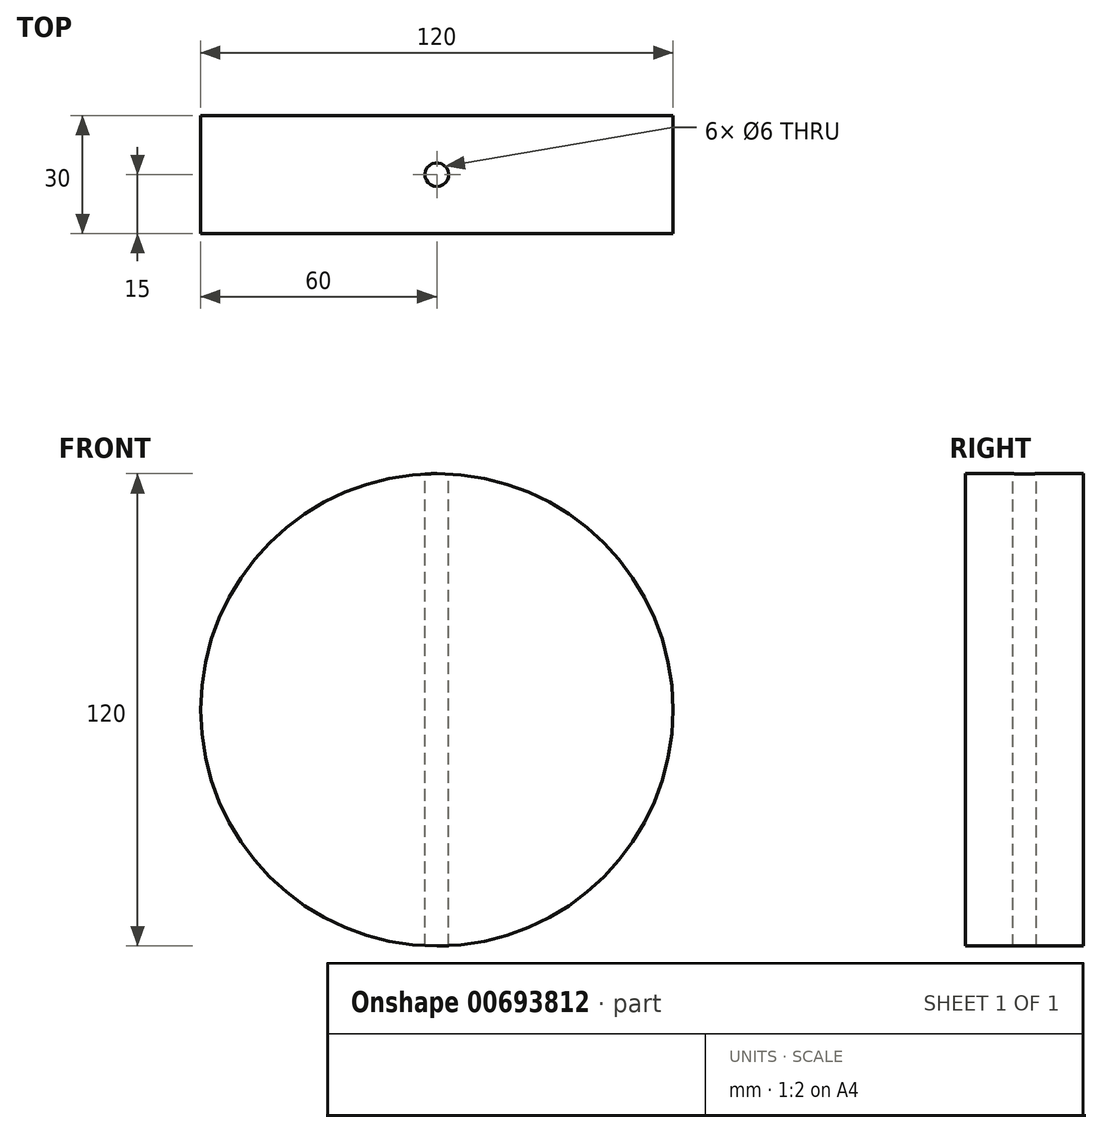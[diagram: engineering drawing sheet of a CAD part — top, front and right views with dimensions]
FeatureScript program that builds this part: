
annotation { "Feature Type Name" : "Feature", "Feature Type Description" : "" }
export const myFeature = defineFeature(function(context is Context, id is Id, definition is map)
    precondition{}
    {
        {
            var Q0;
            Q0=qCreatedBy(makeId("Front.planeOp"),FACE);
            var sketch = newSketch(context, id + "F0", { "sketchPlane" : qUnion([Q0])});
            skCircle(sketch, "E0", {"center": v(0, 0) * mm, "radius": 60 * mm});
            skSolve(sketch);
        }
        {
            var Q0;
            Q0 = qSketchRegion(id + "F0", true);
            extrude(context, id + "F1", {"entities" : qUnion([Q0]), "depth" : 30 * mm, "offsetDistance" : 25 * mm});
        }
        {
            var Q0;
            Q0=qCreatedBy(makeId("Front.planeOp"),FACE);
            cPlane(context, id + "F2", {"entities" : qUnion([Q0]), "cplaneType" : CPlaneType.OFFSET, "offset" : 15 * mm, "width" : 150 * mm, "height" : 150 * mm});
        }
        {
            var Q0;
            Q0=qCreatedBy(id+"F2.planeOp",FACE);
            var sketch = newSketch(context, id + "F3", { "sketchPlane" : qUnion([Q0])});
            skLineSegment(sketch, "E1", {"start": v(0, 68.4) * mm, "end": v(0, -68.77) * mm});
            skSolve(sketch);
        }
        {
            var Q0;
            Q0=qCreatedBy(makeId("Top.planeOp"),FACE);
            var sketch = newSketch(context, id + "F4", { "sketchPlane" : qUnion([Q0])});
            skCircle(sketch, "E2", {"center": v(0, -15) * mm, "radius": 3 * mm});
            skSolve(sketch);
        }
        {
            var Q0;
            Q0 = qSketchRegion(id + "F4", true);
            extrude(context, id + "F5", {"entities" : qUnion([Q0]), "operationType" : NewBodyOperationType.REMOVE, "endBound" : BoundingType.SYMMETRIC, "oppositeDirection" : true, "depth" : 120 * mm, "offsetDistance" : 25 * mm});
        }
    });
